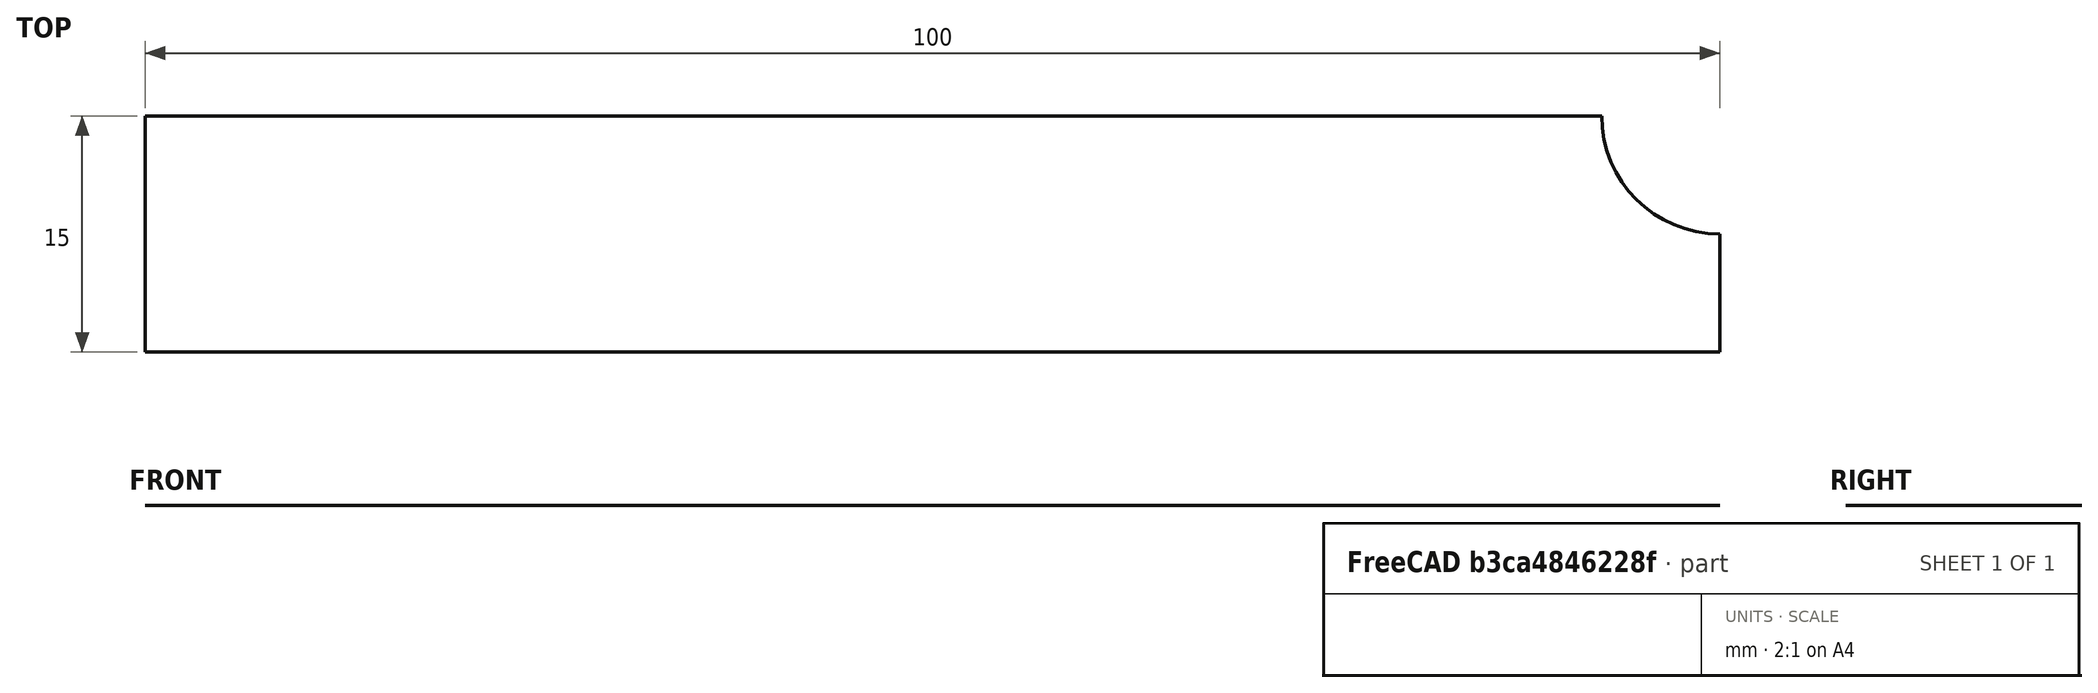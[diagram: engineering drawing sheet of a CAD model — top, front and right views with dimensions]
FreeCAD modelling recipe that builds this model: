
FCSTD DOCUMENT  (FreeCAD 0.20R29410 (Git))
Label: 1-4Model_PerforatedSpecimen
License: All rights reserved
LicenseURL: http://en.wikipedia.org/wiki/All_rights_reserved
objects: Sketcher::SketchObject×1, PartDesign::Body×1, Part::Face×1
note: 3 computed .brp shape members not serialized (recipe doc carries the construction recipe); baked Part::Feature solids carry a one-line shape summary decoded from their .brp

FEATURE [Sketcher::SketchObject] Sketch
  FullyConstrained = true
  MapMode = 5
  Support = -> [XY_Plane]
  sketch-geometry (5):
    g0: LineSegment StartX=-100 StartY=0 StartZ=0 EndX=-7.5 EndY=0 EndZ=0
    g1: LineSegment StartX=0 StartY=-7.5 StartZ=0 EndX=0 EndY=-15 EndZ=0
    g2: LineSegment StartX=0 StartY=-15 StartZ=0 EndX=-100 EndY=-15 EndZ=0
    g3: LineSegment StartX=-100 StartY=-15 StartZ=0 EndX=-100 EndY=0 EndZ=0
    g4: ArcOfCircle CenterX=0 CenterY=0 CenterZ=0 NormalX=0 NormalY=0 NormalZ=1 AngleXU=0 Radius=7.5 StartAngle=3.14159 EndAngle=4.71239
  constraints (15):
    c: PointOnObject(g0,g-1)
    c: PointOnObject(g0,g-1)
    c: PointOnObject(g1,g-2)
    c: PointOnObject(g1,g-2)
    c: Coincident(g1,g2)
    c: Horizontal(g2)
    c: Coincident(g2,g3)
    c: Coincident(g3,g0)
    c: Vertical(g3)
    c: Coincident(g4,g0)
    c: Coincident(g4,g1)
    c: Radius(g4) = 7.5
    c: Coincident(g-1,g4)
    c: DistanceX(g0,g1) = 100
    c: DistanceY(g1,g0) = 15
FEATURE [PartDesign::Body] Body
  Group = -> [Sketch]
  Origin = -> Origin
FEATURE [Part::Face] Face
  FaceMakerClass = Part::FaceMakerBullseye
  Sources = -> [Sketch]
